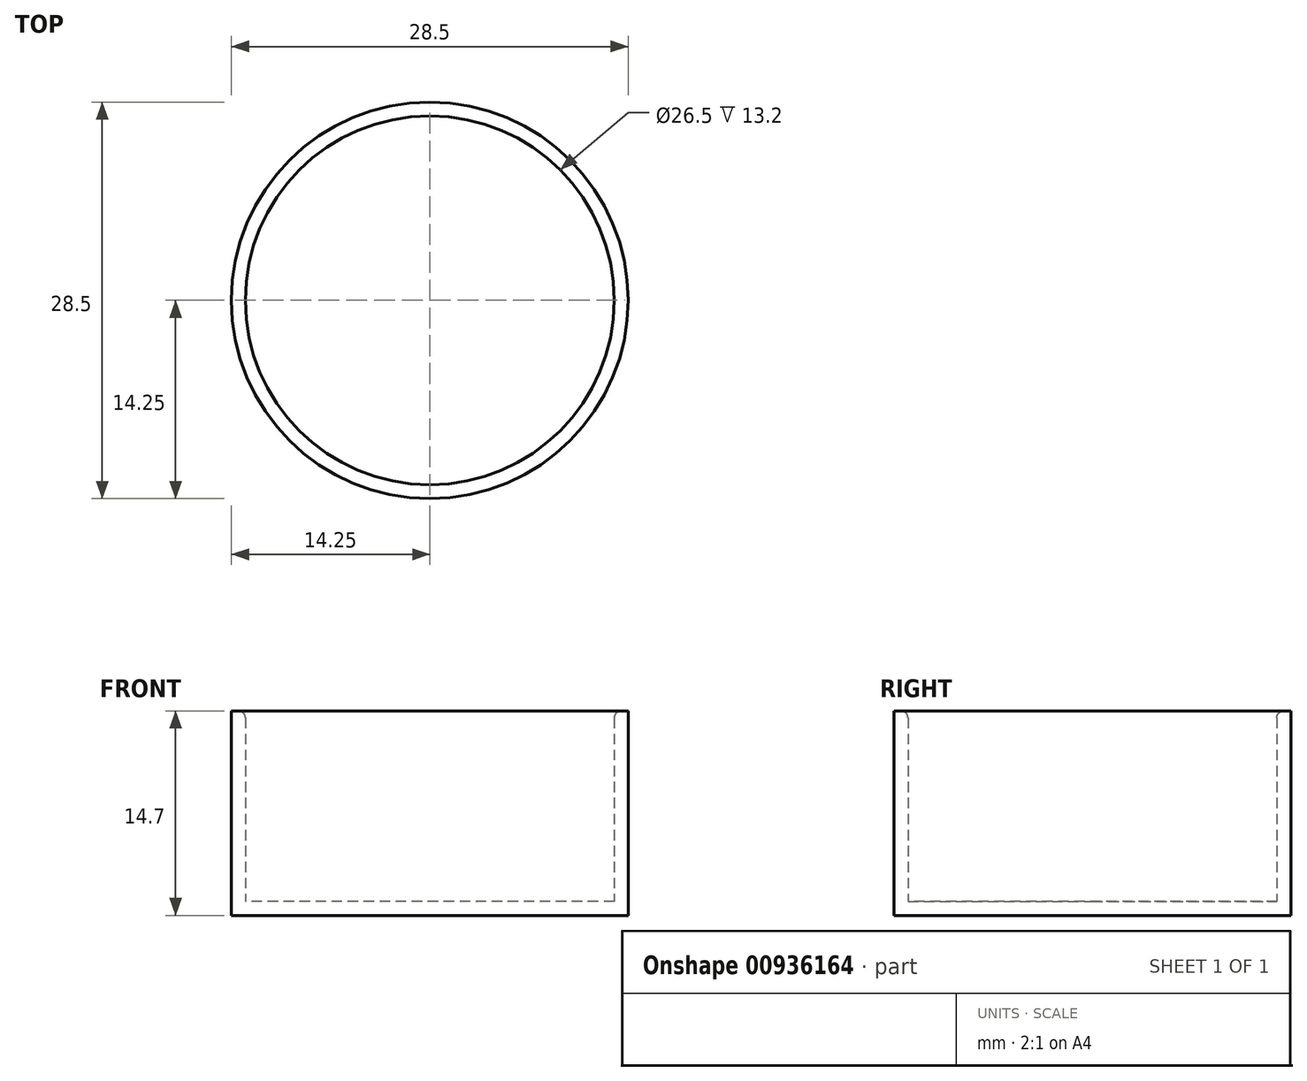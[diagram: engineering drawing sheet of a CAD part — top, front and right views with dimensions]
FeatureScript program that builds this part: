
annotation { "Feature Type Name" : "Feature", "Feature Type Description" : "" }
export const myFeature = defineFeature(function(context is Context, id is Id, definition is map)
    precondition{}
    {
        {
            var Q0;
            Q0=qCreatedBy(makeId("Top.planeOp"),FACE);
            var sketch = newSketch(context, id + "F0", { "sketchPlane" : qUnion([Q0])});
            skCircle(sketch, "E0", {"center": v(0, 0) * mm, "radius": 14.25 * mm});
            skSolve(sketch);
        }
        {
            var Q0;
            Q0 = qSketchRegion(id + "F0", true);
            extrude(context, id + "F1", {"entities" : qUnion([Q0]), "depth" : 14.7 * mm, "offsetDistance" : 25 * mm});
        }
        {
            var Q0;
            Q0=makeQuery(id+"F1.opExtrude","CAP_FACE",FACE,{"disambiguationData":[OSD([sQuery(id+"F0.wireOp",EDGE,"E0")])],"isStart":false});
            shell(context, id + "F2", {"entities" : qUnion([Q0]), "thickness" : 1 * mm});
        }
        {
            var Q0;
            {var subQ0=sQuery(id+"F0.wireOp",EDGE,"E0");Q0=makeQuery(id+"F2.opShell","OFFSET_EDGE",EDGE,{"disambiguationData":[OSD([subQ0]),TDD([makeQuery(id+"F1.opExtrude","CAP_EDGE",EDGE,{"disambiguationData":[OSD([subQ0])],"isStart":false})])]});}
            fillet(context, id + "F3", {"entities" : qUnion([Q0]), "radius" : .5 * mm, "tangentPropagation" : true, "allowEdgeOverflow" : false});
        }
    });
